# Revit family: NLRS_00_AIR_Muurrooster_ST-415_Storax
name_source: partatom
category: Air Terminals
units: mm (PartAtom-declared; Revit-internal decimal feet)

## family parameters
Cut with Voids When Loaded = No
Host = Face
Part Type = Normal
Room Calculation Point = Yes
Round Connector Dimension = Use Diameter
Shared = No

## types (3) — shared parameters
Apparent Load = 0 VA
Assembly Code = 57.10.90.1
Based on = Renson
Default Elevation = 1219 mm
Export Type to IFC As = IfcAirTerminalType
IfcExportAs = IfcAirTerminalType
IfcExportType = Grille
Manufacturer = Storax
RSen_C_code_CBNL = Louvre
RSen_C_code_ETIM = Overstroomrooster
RSen_C_code_gtin = -
RSen_C_depth = 34 mm
RSen_C_material = RSen_h4_aluminum
RSen_C_type = glazed-in louvre
RSen_C_type_comments = glazed-in louvre
STX_I Backframe = No
STX_I BaseKeynote = 57.10.90.1
STX_I Blade_pitch = 33 mm
STX_I Blade_shape = S
STX_I Blade_type = L.033.08
STX_I Burglarproof_RC class = -
STX_I Cd coefficient_discharge = 0.092
STX_I Ce coefficient_intake = 0.09
STX_I Control = -
STX_I Drainage profile = Yes
STX_I Fire resistance = -
STX_I Flange_height = 21 mm  [stored 0.0688976 ft]
STX_I Flange_thickness = 24 mm  [stored 0.0787402 ft]
STX_I Flange_thickness max = 32 mm  [stored 0.104987 ft]
STX_I Flange_thickness min = 24 mm  [stored 0.0787402 ft]
STX_I G4 filter = Yes
STX_I Glazed in = Yes
STX_I Height_max = 4000 mm  [stored 13.1234 ft]
STX_I Height_min = 130 mm  [stored 0.426509 ft]
STX_I IP = IP2XD
STX_I K factor_discharge = 118.15
STX_I K factor_intake = 123.46
STX_I Material = aluminiumAlMgSi0.5
STX_I Puncture proof = Yes
STX_I Removable insect mesh = Yes
STX_I Removable insect mesh_info = Min. dimensions: 190x190 mm; Max. dimensions: 1500x1200 mm
STX_I Shape = rectangular
STX_I Size_maximum = see price list
STX_I Sound reduction_Dw = -
STX_I Sound reduction_Rw = -
STX_I U-value = -
STX_I Visual free area = 0.57
STX_I Water channel = Yes
STX_I Width_max = 4000 mm  [stored 13.1234 ft]
STX_I Width_min = 130 mm  [stored 0.426509 ft]
STX_I Without flange = No
STX_I Without flange_info = no
STX_I Zichtbaar vrije opp. = 0.26
STX_V Air exhaust = No
STX_V Supply air = Yes
STX_W Fingerprint = <RSen_C_length> x <RSen_C_height> mm
Type Comments = glazed-in louvre
Type IFC Predefined Type = Grille
URL = https://www.storax.nl
ZZZ_Airflow_HVACAirflow = 1.0 m³/h
ZZZ_Cut out_depth negative_Length = -500 mm  [stored -1.64042 ft]
ZZZ_Cut out_depth_Length = 500 mm  [stored 1.64042 ft]
ZZZ_Depth negative_Length = -34 mm
ZZZ_Depth_Length = 34 mm
ZZZ_Flange_offset_Length = 27 mm  [stored 0.0885827 ft]
ZZZ_Louvre_insertion point negative_Length = -5 mm  [stored -0.0164042 ft]
ZZZ_Louvre_insertion point_Length = 5 mm  [stored 0.0164042 ft]
ZZZ_Profile bottom_minimum height_Length = 42 mm  [stored 0.137795 ft]
ZZZ_Profile middle_offset_Length = 20 mm  [stored 0.0656168 ft]
ZZZ_Profile top_offset_Length = 73 mm  [stored 0.239501 ft]
ZZZ_Recess depth_Length = 30 mm  [stored 0.0984252 ft]
ZZZ_Recess depth_negative_Length = -30 mm  [stored -0.0984252 ft]
zero-valued in all types: STX_I Backframe_max wall thickness, STX_I Backframe_min wall thickness, STX_I Depth_max, STX_I Depth_min, STX_I Diameter_max, STX_I Diameter_min, ZZZ_Protrusion_Length

## per-type parameters (varying)
| type | ZZZ_Flange_FamilyType_Air Terminals |
| ST-415-24 | GEO_flange_renson : standard |
| ST-415-28 | GEO_flange_renson 28 : standard |
| ST-415-32 | GEO_flange_renson 32 : standard |

note: column(s) folded — value = type name in every type: Description, Model, RSen_C_code_article, RSen_C_description, RSen_C_model

note: [stored X ft] marks values corroborated as IEEE doubles in the binary element streams (Revit-internal decimal feet)

## geometry (parser evidence)
native form markers: Sweep x55
no freeform markers — native parametric forms only
